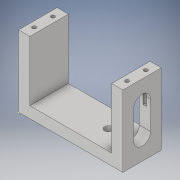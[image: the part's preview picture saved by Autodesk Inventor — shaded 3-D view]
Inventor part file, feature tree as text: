
AUTODESK INVENTOR PART (.ipt)
format: ipt  version: 2019 (Build 230136000, 136)  size: 152,064 bytes
history: native  units: mm
features: sketch x6, extrude x5, other x1
ambient origin geometry x8: Origin, YZ Plane, XZ Plane, XY Plane, X Axis, Y Axis, Z Axis, Center Point
bodies: Body1 (feature_tree)
feature tree (12):
  other  "Твердое тело1"
  extrude  "Выдавливание1"  Depth=38.0mm
  extrude  "Выдавливание2"  Depth=6.0mm
  extrude  "Выдавливание3"  Depth=6.0mm
  extrude  "Выдавливание4"  Depth=6.0mm
  extrude  "Выдавливание5"  Depth=38.0mm
  sketch  "Эскиз6"
  sketch  "Эскиз1"
  sketch  "Эскиз2"
  sketch  "Эскиз3"
  sketch  "Эскиз4"
  sketch  "Эскиз5"
